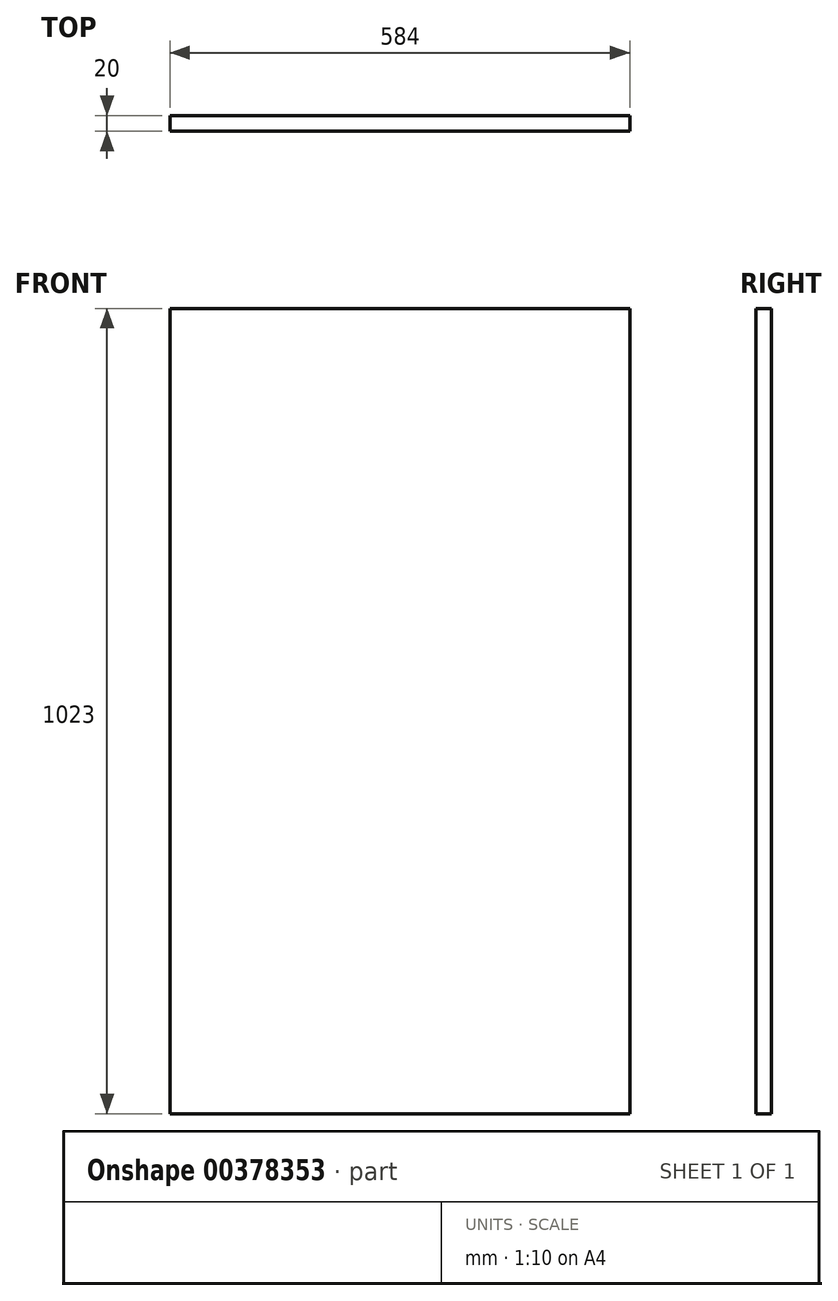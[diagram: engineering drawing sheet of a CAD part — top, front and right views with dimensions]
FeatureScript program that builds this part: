
annotation { "Feature Type Name" : "Feature", "Feature Type Description" : "" }
export const myFeature = defineFeature(function(context is Context, id is Id, definition is map)
    precondition{}
    {
        {
            var Q0;
            Q0=qCreatedBy(makeId("Front.planeOp"),FACE);
            var sketch = newSketch(context, id + "F0", { "sketchPlane" : qUnion([Q0])});
            skLineSegment(sketch, "E0.bottom", {"start": v(292, 511.5) * mm, "end": v(-292, 511.5) * mm});
            skLineSegment(sketch, "E0.top", {"start": v(292, -511.5) * mm, "end": v(-292, -511.5) * mm});
            skLineSegment(sketch, "E0.left", {"start": v(292, 511.5) * mm, "end": v(292, -511.5) * mm});
            skLineSegment(sketch, "E0.right", {"start": v(-292, 511.5) * mm, "end": v(-292, -511.5) * mm});
            skPoint(sketch, "E0.middle", {"position": v(0, 0) * mm});
            skSolve(sketch);
        }
        {
            var Q0;
            Q0 = qSketchRegion(id + "F0", true);
            extrude(context, id + "F1", {"entities" : qUnion([Q0]), "depth" : 20 * mm});
        }
    });
